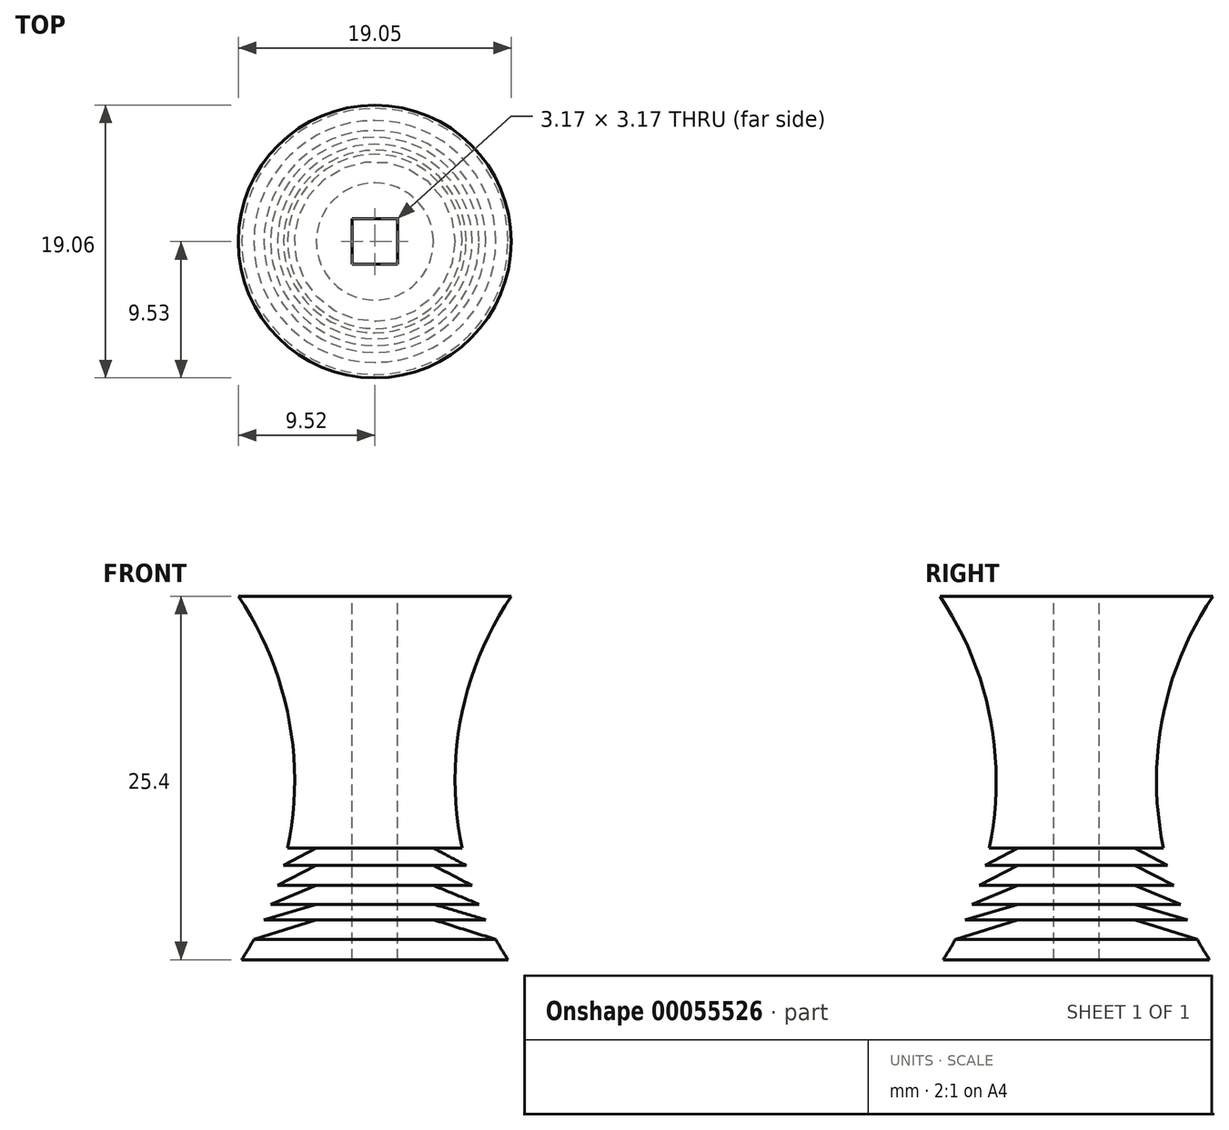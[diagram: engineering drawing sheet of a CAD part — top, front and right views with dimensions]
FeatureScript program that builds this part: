
annotation { "Feature Type Name" : "Feature", "Feature Type Description" : "" }
export const myFeature = defineFeature(function(context is Context, id is Id, definition is map)
    precondition{}
    {
        {
            var Q0;
            Q0=qCreatedBy(makeId("Front.planeOp"),FACE);
            var sketch = newSketch(context, id + "F0", { "sketchPlane" : qUnion([Q0])});
            skLineSegment(sketch, "E0", {"start": v(-44.96, 32.38) * mm, "end": v(-44.96, 6.98) * mm, "construction": true});
            skLineSegment(sketch, "E1", {"start": v(-44.96, 32.38) * mm, "end": v(-54.48, 32.38) * mm});
            skLineSegment(sketch, "E2", {"start": v(-44.96, 6.98) * mm, "end": v(-54.26, 6.98) * mm});
            skLineSegment(sketch, "E3", {"start": v(-44.96, 32.38) * mm, "end": v(-44.96, 6.98) * mm});
            skArc(sketch, "E4", {"start": v(-54.26, 6.98) * mm, "mid": v(-53.82, 7.68) * mm, "end": v(-53.4, 8.4) * mm});
            skLineSegment(sketch, "E5", {"start": v(-51.04, 14.78) * mm, "end": v(-49.05, 14.78) * mm});
            skLineSegment(sketch, "E6", {"start": v(-49.05, 14.78) * mm, "end": v(-51.33, 13.57) * mm});
            skLineSegment(sketch, "E7", {"start": v(-51.33, 13.57) * mm, "end": v(-49.05, 13.57) * mm});
            skLineSegment(sketch, "E8", {"start": v(-49.05, 13.57) * mm, "end": v(-51.75, 12.17) * mm});
            skLineSegment(sketch, "E9", {"start": v(-51.75, 12.17) * mm, "end": v(-49.05, 12.17) * mm});
            skLineSegment(sketch, "E10", {"start": v(-49.05, 12.17) * mm, "end": v(-52.24, 10.86) * mm});
            skLineSegment(sketch, "E11", {"start": v(-52.24, 10.86) * mm, "end": v(-49.05, 10.86) * mm});
            skLineSegment(sketch, "E12", {"start": v(-49.05, 10.86) * mm, "end": v(-52.71, 9.77) * mm});
            skLineSegment(sketch, "E13", {"start": v(-52.71, 9.77) * mm, "end": v(-49.05, 9.77) * mm});
            skLineSegment(sketch, "E14", {"start": v(-49.05, 9.77) * mm, "end": v(-53.4, 8.4) * mm});
            skArc(sketch, "E15.trimOffspring", {"start": v(-51.04, 14.78) * mm, "mid": v(-50.98, 23.93) * mm, "end": v(-54.48, 32.38) * mm});
            skSolve(sketch);
        }
        {
            var Q0;
            Q0 = qSketchRegion(id + "F0", true);
            var Q1;
            Q1=sQuery(id+"F0.wireOp",EDGE,"E3");
            revolve(context, id + "F1", {"entities" : qUnion([Q0]), "axis" : qUnion([Q1]), "revolveType" : RevolveType.FULL});
        }
        {
            var Q0;
            Q0=makeQuery(id+"F1.opRevolve","SWEPT_FACE",FACE,{"disambiguationData":[OSD([sQuery(id+"F0.wireOp",EDGE,"E1")])]});
            var sketch = newSketch(context, id + "F2", { "sketchPlane" : qUnion([Q0])});
            skLineSegment(sketch, "E16.rect.bottom", {"start": v(-43.37, -1.59) * mm, "end": v(-46.55, -1.59) * mm});
            skLineSegment(sketch, "E16.rect.top", {"start": v(-43.37, 1.59) * mm, "end": v(-46.55, 1.59) * mm});
            skLineSegment(sketch, "E16.rect.left", {"start": v(-43.37, -1.59) * mm, "end": v(-43.37, 1.59) * mm});
            skLineSegment(sketch, "E16.rect.right", {"start": v(-46.55, -1.59) * mm, "end": v(-46.55, 1.59) * mm});
            skPoint(sketch, "E16.rect.middle", {"position": v(-44.96, 0) * mm});
            skSolve(sketch);
        }
        {
            var Q0;
            Q0=makeQuery(id+"F2.imprint","IMPRINT",FACE,{"disambiguationData":[TD([[makeQuery(id+"F2.imprint","IMPRINT",EDGE,{"derivedFrom":sQuery(id+"F2.wireOp",EDGE,"E16.rect.bottom")}),-1.0]])]});
            extrude(context, id + "F3", {"entities" : qUnion([Q0]), "operationType" : NewBodyOperationType.REMOVE, "endBound" : BoundingType.THROUGH_ALL, "oppositeDirection" : true, "depth" : 25.4 * mm});
        }
    });
